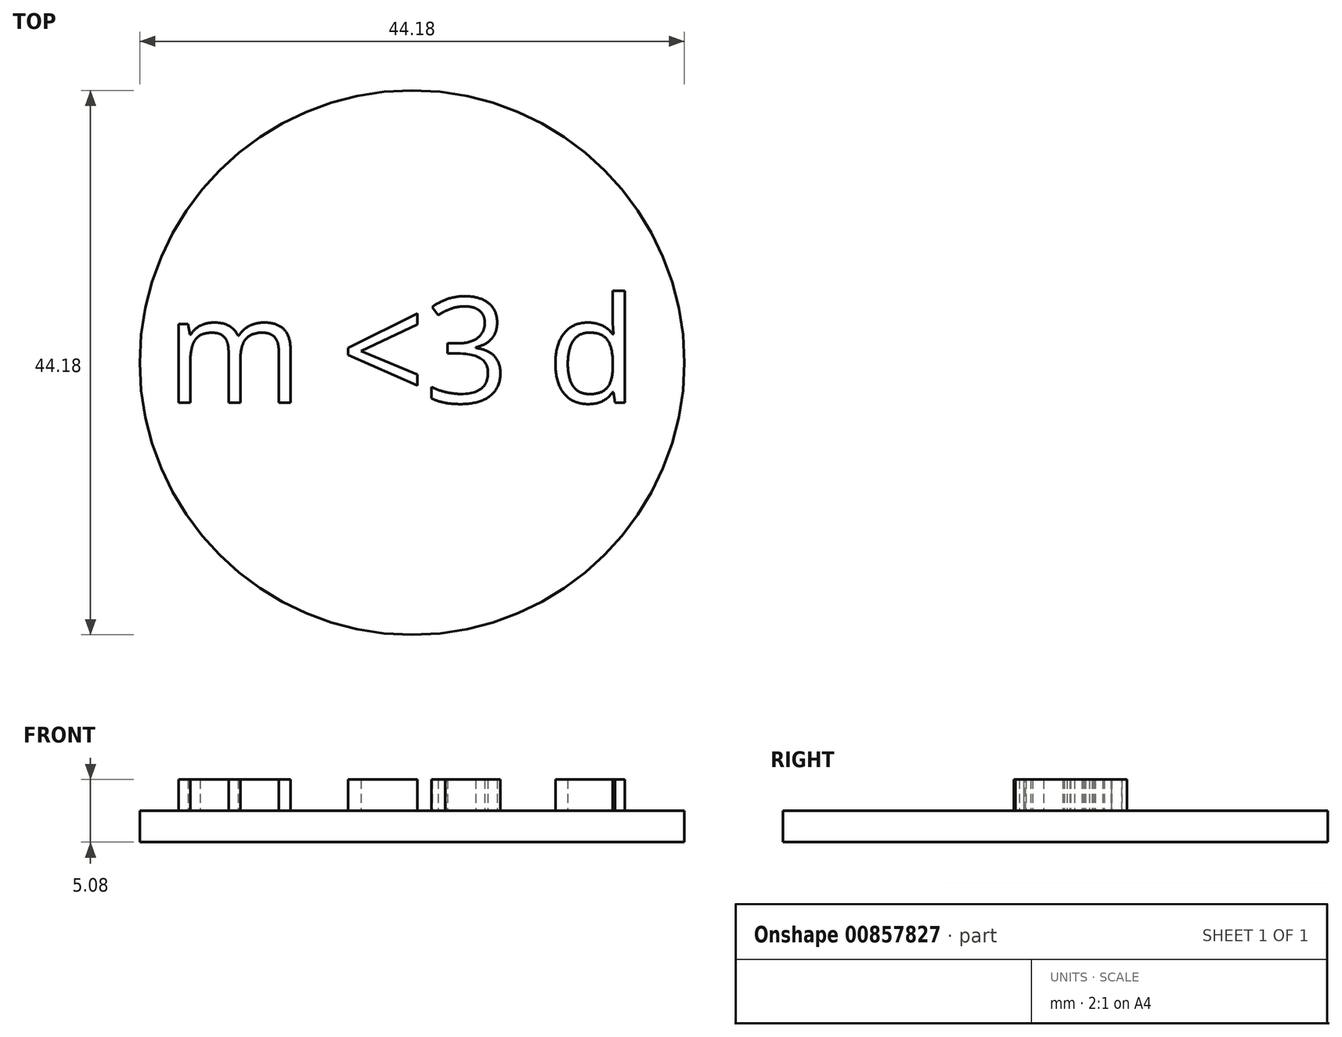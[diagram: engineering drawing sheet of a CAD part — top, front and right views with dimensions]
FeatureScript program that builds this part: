
annotation { "Feature Type Name" : "Feature", "Feature Type Description" : "" }
export const myFeature = defineFeature(function(context is Context, id is Id, definition is map)
    precondition{}
    {
        {
            var Q0;
            Q0=qCreatedBy(makeId("Top.planeOp"),FACE);
            var sketch = newSketch(context, id + "F0", { "sketchPlane" : qUnion([Q0])});
            skCircle(sketch, "E0", {"center": v(0, 0) * mm, "radius": 22.09 * mm});
            skSolve(sketch);
        }
        {
            var Q0;
            Q0=makeQuery(id+"F0.imprint","IMPRINT",FACE,{"disambiguationData":[TD([[makeQuery(id+"F0.imprint","IMPRINT",EDGE,{"derivedFrom":sQuery(id+"F0.wireOp",EDGE,"E0")}),1.0]])]});
            var sketch = newSketch(context, id + "F1", { "sketchPlane" : qUnion([Q0])});
            skSolve(sketch);
        }
        {
            var Q0;
            Q0 = qSketchRegion(id + "FBcPcwM7W7WGMHJ_0", true);
            var Q1;
            Q1 = qSketchRegion(id + "F1", true);
            var Q2;
            Q2=makeQuery(id+"F0.imprint","IMPRINT",FACE,{"disambiguationData":[TD([[makeQuery(id+"F0.imprint","IMPRINT",EDGE,{"derivedFrom":sQuery(id+"F0.wireOp",EDGE,"E0")}),1.0]])]});
            extrude(context, id + "F2", {"entities" : qUnion([Q0, Q1, Q2]), "depth" : 2.54 * mm, "offsetDistance" : 25.4 * mm});
        }
        {
            var Q0;
            Q0=makeQuery(id+"F2.opExtrude","CAP_FACE",FACE,{"disambiguationData":[OSD([sQuery(id+"F0.wireOp",EDGE,"E0")])],"isStart":false});
            var sketch = newSketch(context, id + "F3", { "sketchPlane" : qUnion([Q0])});
            skText(sketch, "E1", { "text": "m <3 d", "fontName": "OpenSans-Regular.ttf"});
            const initialGuessF3  = {"E1": [-0.01998, -0.00325, 1, 0, 0.00859]};
            skSetInitialGuess(sketch, initialGuessF3);
            skSolve(sketch);
        }
        {
            var Q0;
            Q0 = qSketchRegion(id + "F3", true);
            extrude(context, id + "F4", {"entities" : qUnion([Q0]), "operationType" : NewBodyOperationType.ADD, "depth" : 2.54 * mm, "offsetDistance" : 25.4 * mm});
        }
    });
